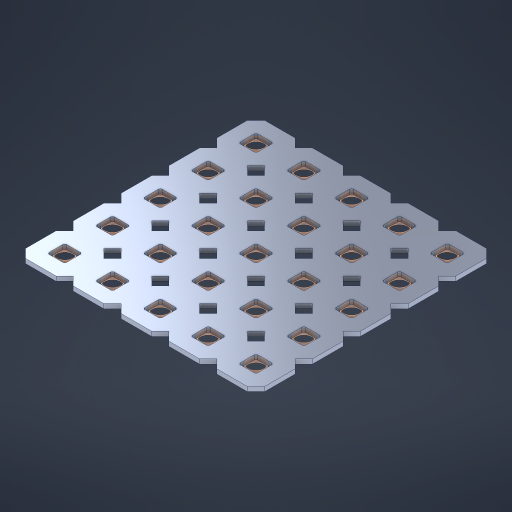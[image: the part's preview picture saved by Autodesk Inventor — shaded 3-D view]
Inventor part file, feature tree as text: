
AUTODESK INVENTOR PART (.ipt)
format: ipt  version: 2023 (Build 270158000, 158)  size: 555,520 bytes
history: native  units: in
note: dims shown in document units (in); Inventor stores cm internally (conversion verified against a paired STEP export)
features: other x26, extrude x24, sketch x2, pattern_linear x1
ambient origin geometry x8: Origin, YZ Plane, XZ Plane, XY Plane, X Axis, Y Axis, Z Axis, Center Point
bodies: Solid1 (feature_tree), Body (feature_tree)
feature tree (53):
  pattern_linear  "Rectangular Pattern1"  Spacing1=0.09in  [1 undecoded]
  sketch  "Sketch1"  dims[d1=0.5in]
  sketch  "Sketch2"  dims[d2=0.182in d3=0.09in d4=0.09in d5=0.09in d6=0.09in d7=0.09in d8=0.09in d9=0.09in d10=0.09in d11=0.02in d13=0.0in d14=0.172in d15=0.0625in d16=0.0in d19=0.5in d22=0.5in]
  other  "Srf1"
  other  "Srf126"
  other  "Srf127"
  other  "Srf128"
  other  "Srf129"
  other  "Srf268"
  other  "Srf269"
  other  "Srf270"
  other  "Srf271"
  other  "Srf272"
  other  "Srf293"
  other  "Srf294"
  other  "Srf295"
  other  "Srf296"
  other  "Srf297"
  other  "Srf318"
  other  "Srf319"
  other  "Srf320"
  other  "Srf321"
  other  "Srf322"
  other  "Srf343"
  other  "Srf344"
  other  "Srf345"
  other  "Srf346"
  other  "Srf347"
  other  "Circle"
  extrude  "ExtrusionSrf126"  Depth=0.09in
  extrude  "ExtrusionSrf127"  Depth=0.09in
  extrude  "ExtrusionSrf128"  Depth=0.09in
  extrude  "ExtrusionSrf129"  Depth=0.09in
  extrude  "ExtrusionSrf268"  Depth=0.09in
  extrude  "ExtrusionSrf269"  Depth=0.09in
  extrude  "ExtrusionSrf270"  Depth=0.09in
  extrude  "ExtrusionSrf271"  Depth=0.02in
  extrude  "ExtrusionSrf272"  TaperAngle=0.0deg  [1 undecoded]
  extrude  "ExtrusionSrf293"  Depth=0.5in
  extrude  "ExtrusionSrf294"  Depth=0.5in TaperAngle=0.0deg
  extrude  "ExtrusionSrf295"  Depth=0.5in
  extrude  "ExtrusionSrf296"  Depth=0.5in
  extrude  "ExtrusionSrf297"  [1 undecoded]
  extrude  "ExtrusionSrf318"  [1 undecoded]
  extrude  "ExtrusionSrf319"  [1 undecoded]
  extrude  "ExtrusionSrf320"  [1 undecoded]
  extrude  "ExtrusionSrf321"  [1 undecoded]
  extrude  "ExtrusionSrf322"  [1 undecoded]
  extrude  "ExtrusionSrf343"  [1 undecoded]
  extrude  "ExtrusionSrf344"  [1 undecoded]
  extrude  "ExtrusionSrf345"  [1 undecoded]
  extrude  "ExtrusionSrf346"  [1 undecoded]
  extrude  "ExtrusionSrf347"  [1 undecoded]
note: 13 required parameter values undecoded (feature->parameter linkage not recoverable at this tier; creation-order binding heuristic only, values carry confidence <= 0.55)
